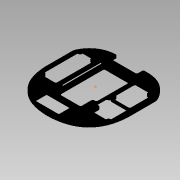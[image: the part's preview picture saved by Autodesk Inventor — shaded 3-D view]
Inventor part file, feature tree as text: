
AUTODESK INVENTOR PART (.ipt)
format: ipt  version: 2015 SP1 (Build 190203100, 203)  size: 601,088 bytes
history: native  units: mm
features: extrude x15, reference x10, sketch x9, fillet x5, projected_geometry x1
ambient origin geometry x8: Origin, YZ Plane, XZ Plane, XY Plane, X Axis, Y Axis, Z Axis, Center Point
bodies: Body1 (feature_tree)
feature tree (40):
  extrude  "Extrusion5"  Depth=75.0mm
  extrude  "Extrusion6"  Depth=65.0mm
  extrude  "Extrusion11"  Depth=130.0mm
  extrude  "Extrusion12"  Depth=40.0mm
  extrude  "Extrusion14"  Depth=4.0mm TaperAngle=0.0deg
  extrude  "Extrusion17"  Depth=48.26mm
  extrude  "Extrusion20"  Depth=48.26mm
  extrude  "Extrusion24"  Depth=20.32mm
  extrude  "Extrusion27"  Depth=3.0mm TaperAngle=0.0deg
  extrude  "Extrusion29"  Depth=2.0mm
  extrude  "Extrusion30"  Depth=2.0mm
  fillet  "Fillet1"  Radius=43.0mm
  extrude  "Extrusion31"  Depth=2.0mm
  fillet  "Fillet2"  Radius=85.0mm
  sketch  "Sketch25"  dims[d47=3.5mm d48=0.0mm d57=48.26mm]
  extrude  "Extrusion32"  Depth=2.0mm TaperAngle=0.0deg
  extrude  "Extrusion33"  Depth=2.0mm
  fillet  "Fillet3"  Radius=32.442mm
  fillet  "Fillet4"  Radius=32.442mm
  extrude  "Extrusion34"  Depth=2.0mm
  fillet  "Fillet5"  Radius=10.0mm
  sketch  "Sketch7"  dims[d13=74.959789mm d14=75.0mm]
  sketch  "Sketch9"  dims[d15=65.0mm d16=65.0mm]
  reference  "Reference3"
  reference  "Reference4"
  reference  "Reference5"
  reference  "Reference6"
  reference  "Reference7"
  sketch  "Sketch13"  dims[d17=149.959789mm d18=130.0mm]
  reference  "Reference15"
  reference  "Reference16"
  reference  "Reference17"
  reference  "Reference18"
  reference  "Reference19"
  sketch  "Sketch18"  dims[d30=3.5mm d31=40.0mm]
  sketch  "Sketch24"  dims[d32=37.5mm d35=4.0mm d36=0.0mm]
  projected_geometry  "Projected Loop9"
  sketch  "Sketch26"  dims[d58=82.55mm d59=48.26mm]
  sketch  "Sketch27"  dims[d60=74.93mm d61=20.32mm]
  sketch  "Sketch28"  dims[d91=10.0mm d92=0.0mm d93=3.0mm d94=0.0mm d99=3.5mm d101=3.5mm d112=43.0mm d113=43.0mm d114=85.0mm d115=85.0mm d116=3.5mm d117=0.0mm d123=32.442mm d124=32.442mm d126=32.442mm d127=20.216mm d128=10.0mm d129=0.0mm d186=10.0mm d187=0.0mm d231=3.91262mm d274=10.0mm d275=0.0mm d294=5.842mm d311=5.0mm d312=5.0mm d313=5.0mm d314=5.0mm d315=10.0mm d316=0.0mm d317=20.825028mm d318=39.875028mm d319=1.332014mm d320=1.332014mm d321=1.332014mm d322=1.332014mm d323=10.412514mm d324=10.412514mm d325=1.332014mm d326=1.332014mm d327=1.332014mm d328=1.332014mm d329=1.332014mm d330=1.332014mm d331=1.332014mm d332=1.332014mm d333=4.662386mm d334=4.662386mm d335=5.510314mm d336=5.510314mm d337=4.662386mm d338=4.662386mm d339=5.510314mm d340=5.510314mm d348=2.0mm d364=2.0mm d370=180.0deg d379=90.0deg d380=90.0deg d381=2.0mm d382=0.0mm d383=10.0mm d384=0.0mm d385=1.0mm d387=3.5mm d388=3.5mm d389=3.5mm d390=3.5mm d391=3.5mm d393=3.5mm d394=2.0mm d395=3.5mm d396=3.5mm d397=2.0mm d398=10.0mm d399=0.0mm d400=10.0mm d401=2.0mm d402=2.0mm d403=3.5mm d404=0.0mm d407=0.0mm d408=180.0deg d409=2.0mm d410=3.0mm d411=0.0mm d412=2.0mm d413=35.0mm d414=1.555402mm d415=1.555402mm d416=10.0mm d417=0.0mm d418=4.0mm d419=4.0mm d420=0.0mm d421=3.0mm d422=2.0mm d423=10.0mm d424=0.0mm d425=2.0mm]
